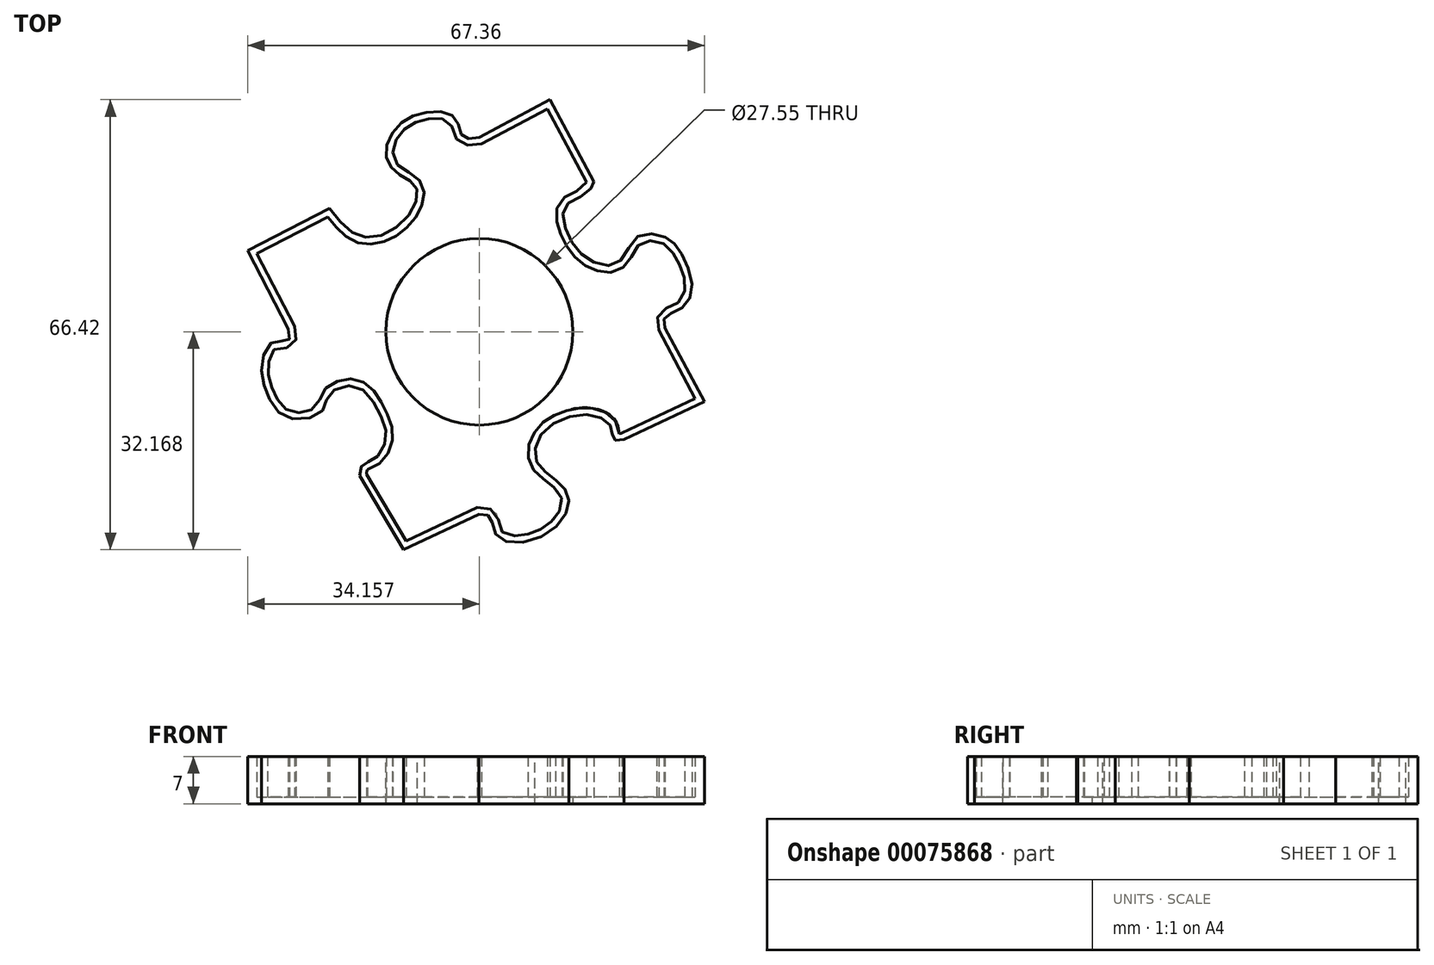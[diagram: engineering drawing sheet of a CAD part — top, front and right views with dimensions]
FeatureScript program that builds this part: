
annotation { "Feature Type Name" : "Feature", "Feature Type Description" : "" }
export const myFeature = defineFeature(function(context is Context, id is Id, definition is map)
    precondition{}
    {
        {
            var Q0;
            Q0=qCreatedBy(makeId("Top.planeOp"),FACE);
            var sketch = newSketch(context, id + "F0", { "sketchPlane" : qUnion([Q0])});
            skLineSegment(sketch, "E0", {"start": v(-38.79, 52.6) * mm, "end": v(-26.7, 58.88) * mm});
            skLineSegment(sketch, "E1", {"start": v(-38.79, 52.6) * mm, "end": v(-32.8, 41.1) * mm});
            skLineSegment(sketch, "E2", {"start": v(-4.64, 69.33) * mm, "end": v(5.8, 74.9) * mm});
            skLineSegment(sketch, "E3", {"start": v(5.8, 74.9) * mm, "end": v(12.27, 62.79) * mm});
            skLineSegment(sketch, "E4", {"start": v(22.76, 41.22) * mm, "end": v(28.57, 30.3) * mm});
            skLineSegment(sketch, "E5", {"start": v(16.72, 24.73) * mm, "end": v(28.57, 30.3) * mm});
            skLineSegment(sketch, "E6", {"start": v(-15.8, 8.48) * mm, "end": v(-4.69, 13.7) * mm});
            skLineSegment(sketch, "E7", {"start": v(-22.3, 19.4) * mm, "end": v(-15.8, 8.48) * mm});
            skFitSpline(sketch, "E8", {"points": [v(-26.7, 58.88) * mm, v(-21.73, 54.62) * mm, v(-15.46, 57.32) * mm, v(-13.98, 62) * mm, v(-16.81, 64.09) * mm, v(-18.41, 66.92) * mm, v(-16.69, 70.98) * mm, v(-12.26, 73.07) * mm, v(-8.2, 72.2) * mm, v(-7.1, 69.5) * mm, v(-4.64, 69.33) * mm], "startDerivative": vector(35.97, -47.12) * mm, "endDerivative": vector(38.84, 6.58) * mm});
            skFitSpline(sketch, "E9", {"points": [v(16.72, 24.73) * mm, v(15.18, 24.73) * mm, v(14.8, 26.57) * mm, v(11.48, 28.41) * mm, v(4.84, 25.95) * mm, v(3.86, 21.4) * mm, v(7.18, 18.32) * mm, v(8.53, 15.12) * mm, v(4.6, 10.45) * mm, v(-1.93, 10.33) * mm, v(-3.03, 13.28) * mm, v(-4.69, 13.7) * mm], "startDerivative": vector(-33.38, -7.34) * mm, "endDerivative": vector(-32.5, -0.82) * mm});
            skFitSpline(sketch, "E10", {"points": [v(-32.8, 41.1) * mm, v(-32.8, 39.36) * mm, v(-34.9, 39.24) * mm, v(-36.74, 35.92) * mm, v(-35.88, 31.36) * mm, v(-32.8, 27.92) * mm, v(-27.89, 28.9) * mm, v(-26.78, 31.36) * mm, v(-22.84, 32.6) * mm, v(-19.52, 28.9) * mm, v(-18.41, 24.84) * mm, v(-20.26, 21.77) * mm, v(-21.86, 21.03) * mm, v(-22.3, 19.4) * mm], "startDerivative": vector(8.96, -40.69) * mm, "endDerivative": vector(-2.76, -35.57) * mm});
            skFitSpline(sketch, "E11", {"points": [v(22.76, 41.22) * mm, v(22.76, 42.8) * mm, v(25.26, 44.16) * mm, v(26.74, 47.48) * mm, v(24.9, 52.65) * mm, v(22.76, 54.62) * mm, v(18.62, 54.62) * mm, v(15.8, 50.8) * mm, v(11.48, 51.3) * mm, v(8.4, 55.1) * mm, v(8.04, 59.17) * mm, v(11.48, 61.38) * mm, v(12.27, 62.79) * mm, v(12.27, 61.75) * mm], "startDerivative": vector(-8.57, 33.37) * mm, "endDerivative": vector(-1.67, -36.34) * mm});
            skSolve(sketch);
        }
        {
            var Q0;
            Q0=makeQuery(id+"F0.imprint","IMPRINT",FACE,{"disambiguationData":[TD([[makeQuery(id+"F0.imprint","IMPRINT",EDGE,{"derivedFrom":sQuery(id+"F0.wireOp",EDGE,"E0")}),-1.0]])]});
            extrude(context, id + "F1", {"entities" : qUnion([Q0]), "depth" : 7 * mm});
        }
        {
            var Q0;
            Q0=makeQuery(id+"F1.opExtrude","CAP_FACE",FACE,{"disambiguationData":[OSD([sQuery(id+"F0.wireOp",EDGE,"E0"),sQuery(id+"F0.wireOp",EDGE,"E1"),sQuery(id+"F0.wireOp",EDGE,"E2"),sQuery(id+"F0.wireOp",EDGE,"E3"),sQuery(id+"F0.wireOp",EDGE,"E4"),sQuery(id+"F0.wireOp",EDGE,"E5"),sQuery(id+"F0.wireOp",EDGE,"E6"),sQuery(id+"F0.wireOp",EDGE,"E7"),sQuery(id+"F0.wireOp",EDGE,"E8"),sQuery(id+"F0.wireOp",EDGE,"E9"),sQuery(id+"F0.wireOp",EDGE,"E10"),sQuery(id+"F0.wireOp",EDGE,"E11")])],"isStart":false});
            shell(context, id + "F2", {"entities" : qUnion([Q0]), "thickness" : 1 * mm});
        }
        {
            var Q0;
            Q0=makeQuery(id+"F0.imprint","IMPRINT",FACE,{"disambiguationData":[TD([[makeQuery(id+"F0.imprint","IMPRINT",EDGE,{"derivedFrom":sQuery(id+"F0.wireOp",EDGE,"E0")}),-1.0]])]});
            var sketch = newSketch(context, id + "F3", { "sketchPlane" : qUnion([Q0])});
            skCircle(sketch, "E12", {"center": v(-4.63, 40.65) * mm, "radius": 13.78 * mm});
            skSolve(sketch);
        }
        {
            var Q0;
            Q0 = qSketchRegion(id + "F3", true);
            extrude(context, id + "F4", {"entities" : qUnion([Q0]), "operationType" : NewBodyOperationType.REMOVE, "depth" : 9.46 * mm});
        }
    });
